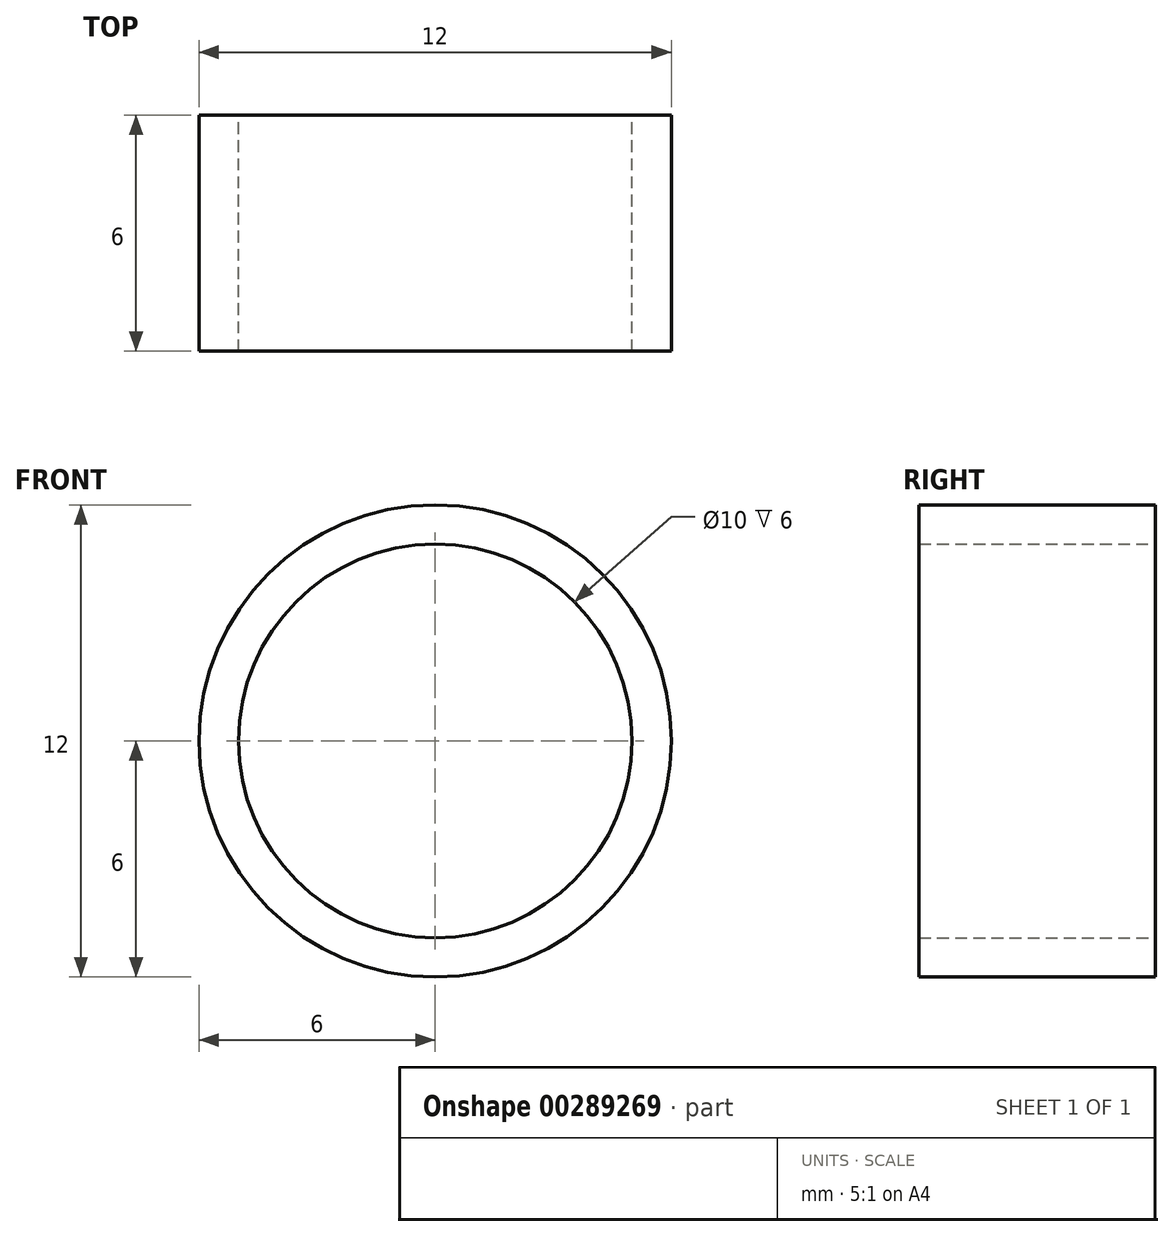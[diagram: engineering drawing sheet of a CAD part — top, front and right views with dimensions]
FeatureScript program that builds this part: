
annotation { "Feature Type Name" : "Feature", "Feature Type Description" : "" }
export const myFeature = defineFeature(function(context is Context, id is Id, definition is map)
    precondition{}
    {
        {
            var Q0;
            Q0=qCreatedBy(makeId("Front.planeOp"),FACE);
            var sketch = newSketch(context, id + "F0", { "sketchPlane" : qUnion([Q0])});
            skCircle(sketch, "E0", {"center": v(0, 0) * mm, "radius": 5 * mm});
            skCircle(sketch, "E1", {"center": v(0, 0) * mm, "radius": 6 * mm});
            skSolve(sketch);
        }
        {
            var Q0;
            Q0=makeQuery(id+"F0.imprint","IMPRINT",FACE,{"disambiguationData":[TD([[makeQuery(id+"F0.imprint","IMPRINT",EDGE,{"derivedFrom":sQuery(id+"F0.wireOp",EDGE,"E0")}),-1.0]])]});
            extrude(context, id + "F1", {"entities" : qUnion([Q0]), "depth" : 6 * mm});
        }
    });
